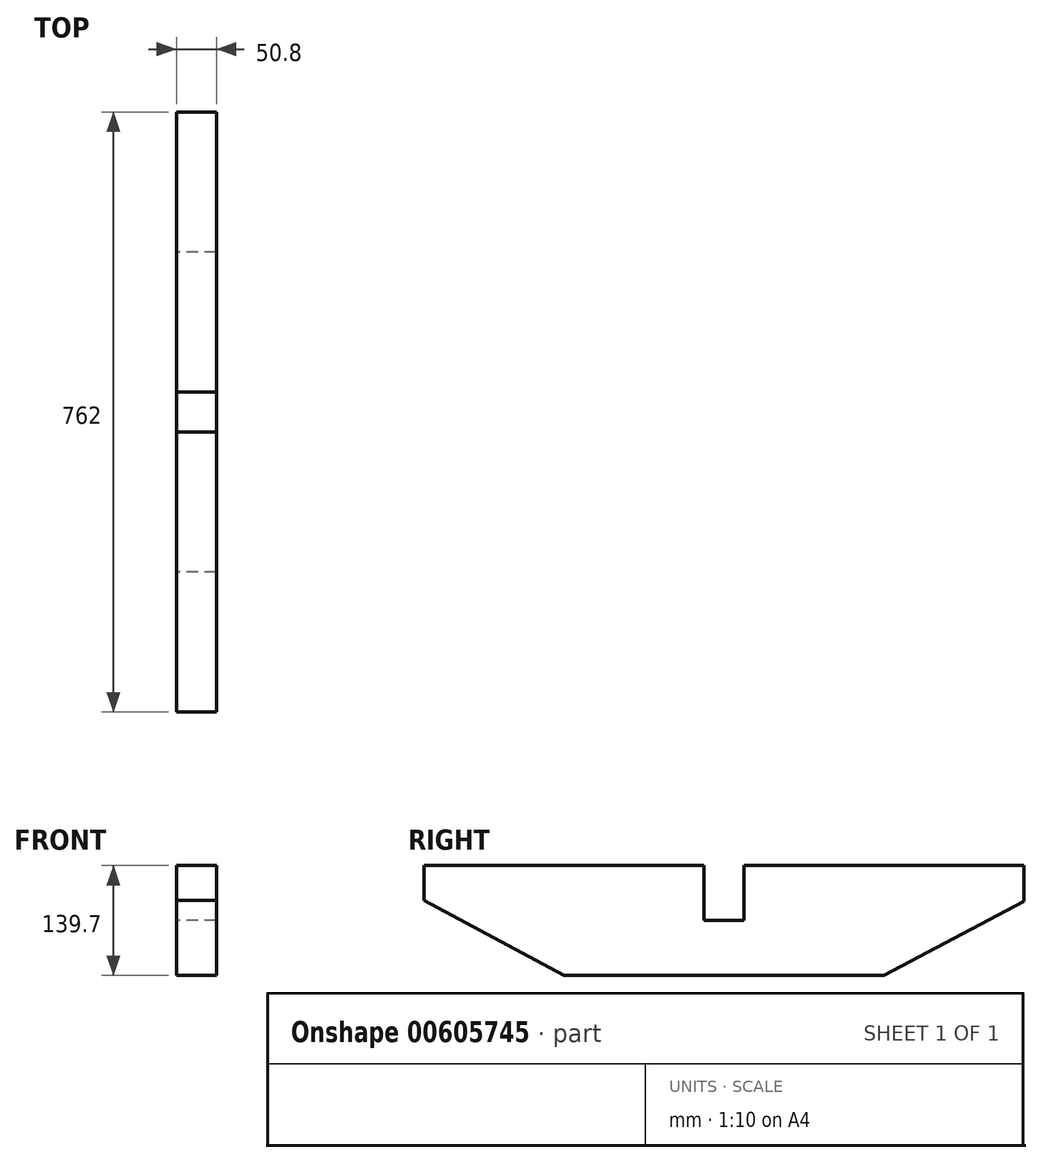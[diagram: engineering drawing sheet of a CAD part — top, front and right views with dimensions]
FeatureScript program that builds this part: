
annotation { "Feature Type Name" : "Feature", "Feature Type Description" : "" }
export const myFeature = defineFeature(function(context is Context, id is Id, definition is map)
    precondition{}
    {
        {
            var Q0;
            Q0=qCreatedBy(makeId("Right.planeOp"),FACE);
            var sketch = newSketch(context, id + "F0", { "sketchPlane" : qUnion([Q0])});
            skLineSegment(sketch, "E0.bottom", {"start": v(-25.4, -72.6) * mm, "end": v(-203.2, -72.6) * mm});
            skLineSegment(sketch, "E0.top", {"start": v(-25.4, 67.1) * mm, "end": v(-381, 67.1) * mm});
            skLineSegment(sketch, "E0.left", {"start": v(-25.4, -72.6) * mm, "end": v(-25.4, 67.1) * mm});
            skLineSegment(sketch, "E0.right", {"start": v(-381, 22.47) * mm, "end": v(-381, 67.1) * mm});
            skPoint(sketch, "E0.middle", {"position": v(-203.2, -2.75) * mm});
            skLineSegment(sketch, "E1.bottom", {"start": v(25.4, 67.1) * mm, "end": v(381, 67.1) * mm});
            skLineSegment(sketch, "E1.top", {"start": v(25.4, -72.6) * mm, "end": v(203.2, -72.6) * mm});
            skLineSegment(sketch, "E1.left", {"start": v(25.4, 67.1) * mm, "end": v(25.4, -72.6) * mm});
            skLineSegment(sketch, "E1.right", {"start": v(381, 67.1) * mm, "end": v(381, 21.51) * mm});
            skPoint(sketch, "E1.middle", {"position": v(203.2, -2.75) * mm});
            skLineSegment(sketch, "E2.top", {"start": v(-25.4, -2.75) * mm, "end": v(25.4, -2.75) * mm});
            skLineSegment(sketch, "E2.right", {"start": v(25.4, 67.1) * mm, "end": v(25.4, -2.75) * mm});
            skLineSegment(sketch, "E3", {"start": v(381, 21.51) * mm, "end": v(203.2, -72.6) * mm});
            skLineSegment(sketch, "E4", {"start": v(-381, 22.47) * mm, "end": v(-203.2, -72.6) * mm});
            skPoint(sketch, "E5.orphan", {"position": v(-381, -72.6) * mm});
            skPoint(sketch, "E6.orphan", {"position": v(381, -72.6) * mm});
            skLineSegment(sketch, "E7.top", {"start": v(-25.4, -72.6) * mm, "end": v(25.4, -72.6) * mm});
            skSolve(sketch);
        }
        {
            var Q0;
            Q0 = qSketchRegion(id + "F0", true);
            extrude(context, id + "F1", {"entities" : qUnion([Q0]), "depth" : 50.8 * mm, "offsetDistance" : 25.4 * mm});
        }
    });
